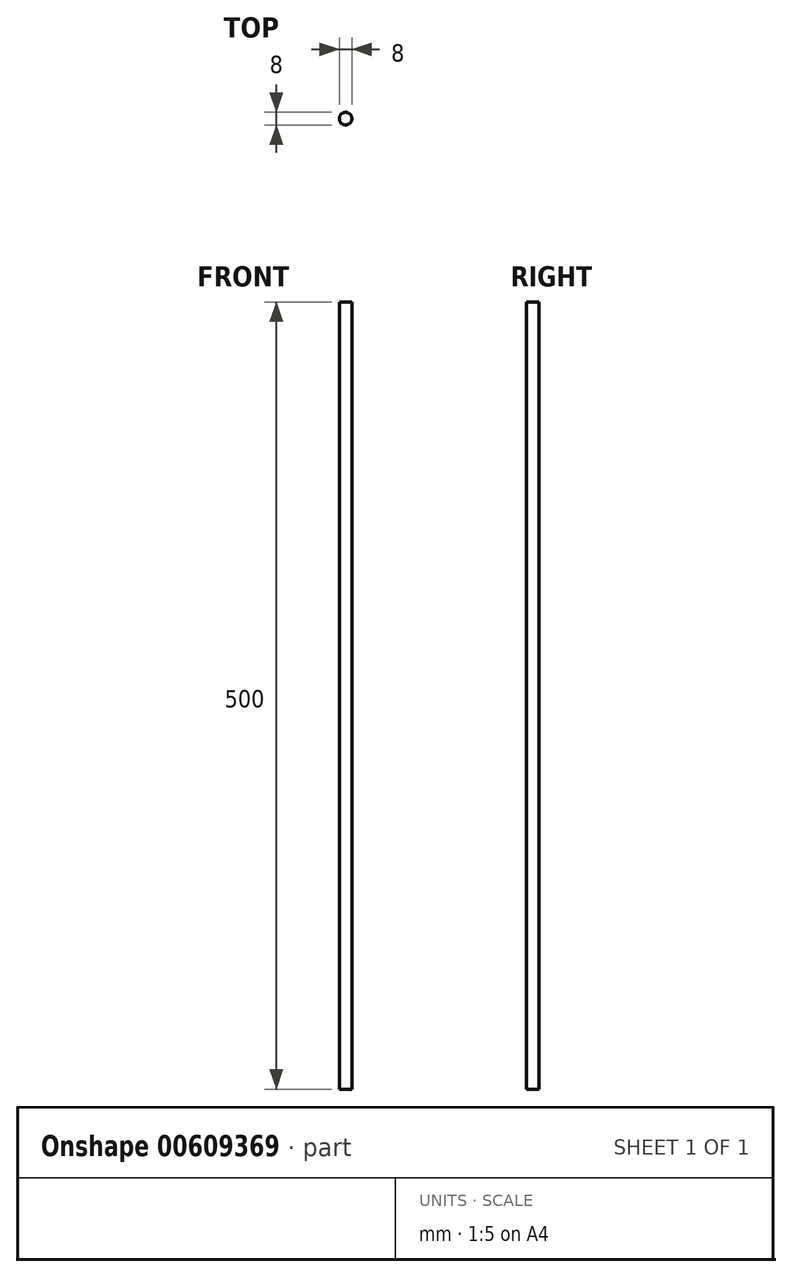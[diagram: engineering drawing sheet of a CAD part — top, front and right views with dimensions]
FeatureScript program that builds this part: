
annotation { "Feature Type Name" : "Feature", "Feature Type Description" : "" }
export const myFeature = defineFeature(function(context is Context, id is Id, definition is map)
    precondition{}
    {
        {
            var Q0;
            Q0=qCreatedBy(makeId("Top.planeOp"),FACE);
            var sketch = newSketch(context, id + "F0", { "sketchPlane" : qUnion([Q0])});
            skCircle(sketch, "E0", {"center": v(0, 0) * mm, "radius": 4 * mm});
            skSolve(sketch);
        }
        {
            var Q0;
            Q0 = qSketchRegion(id + "F0", true);
            extrude(context, id + "F1", {"entities" : qUnion([Q0]), "depth" : 500 * mm, "offsetDistance" : 25 * mm});
        }
    });
